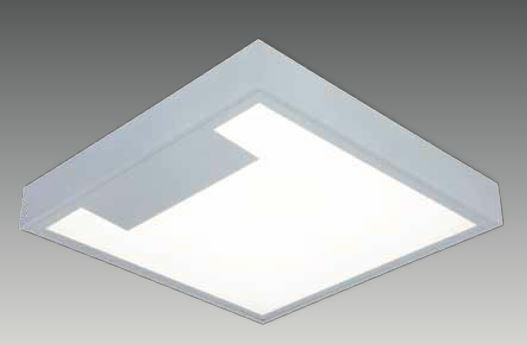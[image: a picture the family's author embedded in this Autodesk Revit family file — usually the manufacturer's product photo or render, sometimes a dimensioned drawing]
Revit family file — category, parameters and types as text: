
# Revit family: SD 6060 MIR
name_source: partatom
category: Lighting Fixtures
revit_build: Autodesk Revit 2017 (Build: 20160225_1515(x64)
units: mm (PartAtom-declared; Revit-internal decimal feet)

## family parameters
Cut with Voids When Loaded = No
Host = Face
Light Source = Yes
Part Type = Normal
Room Calculation Point = No
Round Connector Dimension = Use Diameter
Shared = No

## types (4) — shared parameters
Color Filter = 16777215
Default Elevation = 1219 mm
Dimming Lamp Color Temperature Shift = <None>
Emit Shape Visible in Rendering = Yes
Emit from Rectangle Length = 570 mm  [stored 1.87008 ft]
Emit from Rectangle Width = 570 mm  [stored 1.87008 ft]
Light Source Symbol Size = 610 mm
Manufacturer = ARLIGHT
Type Image = SD 6060 MIR.JPG

## per-type parameters (varying)
| type | Wattage Comments |
| SDMIR.6060.36.30 | 36 |
| SDMIR.6060.36.40 | 36 |
| SDMIR.6060.28.30 | 28 |
| SDMIR.6060.28.40 | 28 |

note: [stored X ft] marks values corroborated as IEEE doubles in the binary element streams (Revit-internal decimal feet)

## geometry (parser evidence)
native form markers: Sweep x2
no freeform markers — native parametric forms only
